# Revit family: Drain_Floor_Round-Zurn-Z415H-LR
name_source: partatom
category: Plumbing Fixtures
units: mm (PartAtom-declared; Revit-internal decimal feet)

## family parameters
Always vertical = Yes
Cut with Voids When Loaded = No
Maintain Annotation Orientation = No
OmniClass Number = 23.70.50.21.24.14
OmniClass Title = Deck Waste Water Drains
Part Type = Normal
Room Calculation Point = No
Round Connector Dimension = Use Radius
Shared = No
Work Plane-Based = No

## types (9) — shared parameters
Approx. Wt. Lbs. = 13.00 lb
Assembly Code = D2030300
CW Connection = No
Default Elevation = 30 "
Description = BODY ASSEMBLY W/ “TYPE H” CLAMP DEVICE AND “TYPE LR” LIGATURE RESISTATANT STRAINER
Grate Radius = 2.7 "
HW Connection = No
Manufacturer = Zurn Water, LLC
Manufacurer Brand = Zurn
Material Main = Iron - Zurn - Cast - Painted - Blue
Model = ZN415H-LR
Modified Date = 02/12/2026
Product Documentation Link = https://files.zurn.com
Product Installation Sheet URL = https://files.zurn.com
Product Page URL = https://www.zurn.com
Product data url = https://www.bimobject.com
Strainer Diameter (B) = 6 "
Strainer Material = Bronze - Zurn - Polished Nickel
Strainer Open Area = 1.9 in²
URL = www.zurn.com
Vent Connection = No
Waste Connection = Yes
zero-valued in all types: CWFU, HWFU, WFU

## per-type parameters (varying)
| type | Body Height (E) | Pipe Size 'A' (Inner Diameter) | Pipe Size 'A' (Inner Radius) | Pipe Size 'A' (Nominal Diameter) | Pipe Size 'A' (Nominal Radius) | Pipe Size 'A' (Outer Diameter) | Pipe Size 'A' (Outer Radius) | Type Comments |
| ZN415H-LR-2IP-6B | 2.438 " | 2.067 " | 1.034 " | 2 " | 1 " | 2.375 " | 1.188 " | ZN415H-LR with 6 Inch Strainer and 2 Inch IP Threaed Outlet |
| ZN415H-LR-3IP-6B | 2.75 " | 3.068 " | 1.534 " | 3 " | 1.5 " | 3.5 " | 1.75 " | ZN415H-LR with 6 Inch Strainer and 3 Inch IP Threaed Outlet |
| ZN415H-LR-4IP-6B | 2.813 " | 4.026 " | 2.013 " | 4 " | 2 " | 4.5 " | 2.25 " | ZN415H-LR with 6 Inch Strainer and 4 Inch IP Threaed Outlet |
| ZN415H-LR-2NH-6B | 3.813 " | 2.067 " | 1.034 " | 2 " | 1 " | 2.375 " | 1.188 " | ZN415H-LR with 6 Inch Strainer and 2 Inch No-Hub Outlet |
| ZN415H-LR-3NH-6B | 3.813 " | 3.068 " | 1.534 " | 3 " | 1.5 " | 3.5 " | 1.75 " | ZN415H-LR with 6 Inch Strainer and 3 Inch No-Hub Outlet |
| ZN415H-LR-4NH-6B | 3.813 " | 4.026 " | 2.013 " | 4 " | 2 " | 4.5 " | 2.25 " | ZN415H-LR with 6 Inch Strainer and 4 Inch No-Hub Outlet |
| ZN415H-LR-2NL-6B | 3.875 " | 2.067 " | 1.034 " | 2 " | 1 " | 2.375 " | 1.188 " | ZN415H-LR with 6 Inch Strainer and 2 Inch Neo-Loc Outlet |
| ZN415H-LR-3NL-6B | 3.875 " | 3.026 " | 1.513 " | 3 " | 1.5 " | 3.5 " | 1.75 " | ZN415H-LR with 6 Inch Strainer and 3 Inch Neo-Loc Outlet |
| ZN415H-LR-4NL-6B | 3.875 " | 4.026 " | 2.013 " | 4 " | 2 " | 4.5 " | 2.25 " | ZN415H-LR with 6 Inch Strainer and 4 Inch Neo-Loc Outlet |

## geometry (parser evidence)
native form markers: Sweep x4
no freeform markers — native parametric forms only
